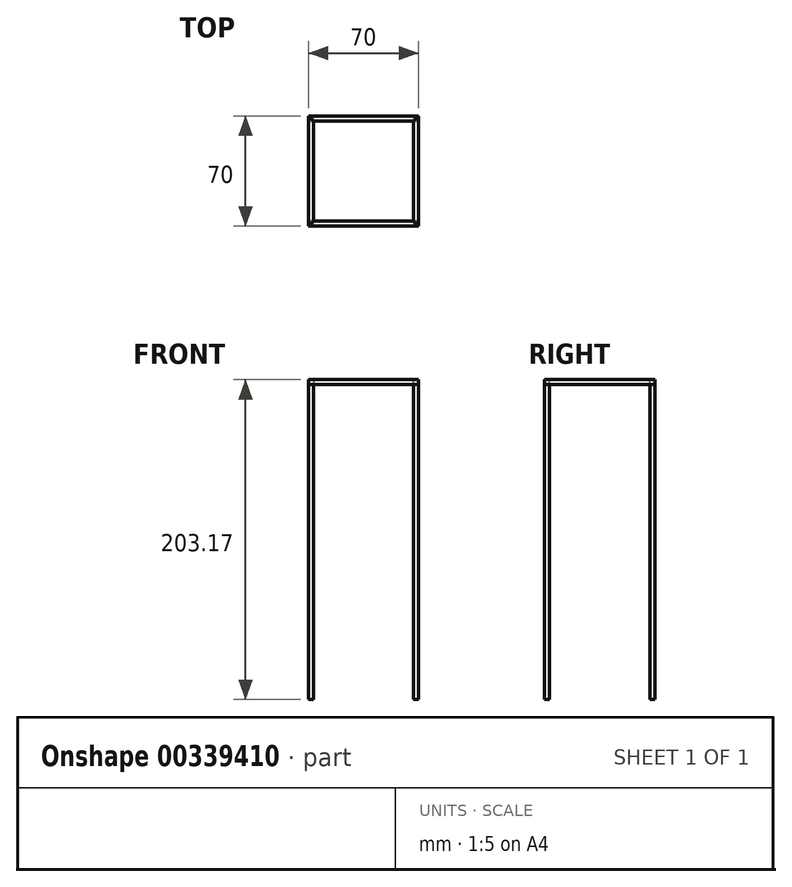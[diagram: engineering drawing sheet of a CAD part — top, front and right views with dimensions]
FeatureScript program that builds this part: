
annotation { "Feature Type Name" : "Feature", "Feature Type Description" : "" }
export const myFeature = defineFeature(function(context is Context, id is Id, definition is map)
    precondition{}
    {
        {
            var Q0;
            Q0=qCreatedBy(makeId("Front.planeOp"),FACE);
            var sketch = newSketch(context, id + "F0", { "sketchPlane" : qUnion([Q0])});
            skLineSegment(sketch, "E0.bottom", {"start": v(0, 200) * mm, "end": v(3.17, 200) * mm});
            skLineSegment(sketch, "E0.top", {"start": v(0, 0) * mm, "end": v(3.18, 0) * mm});
            skLineSegment(sketch, "E0.left", {"start": v(0, 200) * mm, "end": v(0, 0) * mm});
            skLineSegment(sketch, "E0.right", {"start": v(3.18, 200) * mm, "end": v(3.18, 0) * mm});
            skLineSegment(sketch, "E1.bottom", {"start": v(0, 203.18) * mm, "end": v(70, 203.18) * mm});
            skLineSegment(sketch, "E1.top", {"start": v(0, 200) * mm, "end": v(70, 200) * mm});
            skLineSegment(sketch, "E1.left", {"start": v(0, 203.18) * mm, "end": v(0, 200) * mm});
            skLineSegment(sketch, "E1.right", {"start": v(70, 203.18) * mm, "end": v(70, 200) * mm});
            skLineSegment(sketch, "E2", {"start": v(66.83, 200) * mm, "end": v(66.83, 0) * mm});
            skLineSegment(sketch, "E3", {"start": v(3.17, 196.8) * mm, "end": v(66.83, 190.43) * mm});
            skLineSegment(sketch, "E4", {"start": v(3.18, 200) * mm, "end": v(66.82, 193.62) * mm});
            skLineSegment(sketch, "E5", {"start": v(66.82, 193.62) * mm, "end": v(66.82, 190.43) * mm});
            skLineSegment(sketch, "E6", {"start": v(3.18, 196.8) * mm, "end": v(3.18, 200) * mm});
            skLineSegment(sketch, "E7", {"start": v(3.18, 100) * mm, "end": v(66.83, 100) * mm});
            skLineSegment(sketch, "E8", {"start": v(66.83, 103.17) * mm, "end": v(66.83, 100) * mm});
            skLineSegment(sketch, "E9", {"start": v(3.18, 100) * mm, "end": v(3.18, 103.17) * mm});
            skLineSegment(sketch, "E10", {"start": v(3.18, 183.7) * mm, "end": v(66.82, 151.36) * mm});
            skLineSegment(sketch, "E11", {"start": v(3.17, 187.25) * mm, "end": v(66.83, 154.92) * mm});
            skLineSegment(sketch, "E12", {"start": v(66.83, 154.92) * mm, "end": v(66.83, 151.36) * mm});
            skLineSegment(sketch, "E13", {"start": v(3.18, 183.7) * mm, "end": v(3.18, 187.25) * mm});
            skLineSegment(sketch, "E14.bottom", {"start": v(3.17, 190.43) * mm, "end": v(66.82, 190.43) * mm});
            skLineSegment(sketch, "E14.top", {"start": v(3.17, 187.25) * mm, "end": v(66.83, 187.25) * mm});
            skLineSegment(sketch, "E14.left", {"start": v(66.83, 190.43) * mm, "end": v(66.83, 187.25) * mm});
            skLineSegment(sketch, "E14.right", {"start": v(3.18, 190.43) * mm, "end": v(3.18, 187.25) * mm});
            skLineSegment(sketch, "E15.bottom", {"start": v(3.18, 144.4) * mm, "end": v(66.83, 103.18) * mm});
            skLineSegment(sketch, "E15.top", {"start": v(3.18, 148.18) * mm, "end": v(66.83, 106.96) * mm});
            skLineSegment(sketch, "E15.left", {"start": v(66.83, 106.96) * mm, "end": v(66.83, 103.17) * mm});
            skLineSegment(sketch, "E15.right", {"start": v(3.18, 148.18) * mm, "end": v(3.18, 144.4) * mm});
            skLineSegment(sketch, "E16.bottom", {"start": v(3.18, 148.18) * mm, "end": v(66.83, 148.18) * mm});
            skLineSegment(sketch, "E16.top", {"start": v(3.18, 151.36) * mm, "end": v(66.83, 151.36) * mm});
            skLineSegment(sketch, "E16.left", {"start": v(3.18, 151.36) * mm, "end": v(3.18, 148.18) * mm});
            skLineSegment(sketch, "E16.right", {"start": v(66.83, 151.36) * mm, "end": v(66.83, 148.18) * mm});
            skLineSegment(sketch, "E17", {"start": v(3.18, 103.17) * mm, "end": v(66.83, 103.17) * mm});
            skLineSegment(sketch, "E18", {"start": v(3.18, 100) * mm, "end": v(66.83, 8.34) * mm});
            skLineSegment(sketch, "E19", {"start": v(3.18, 100) * mm, "end": v(3.18, 91.66) * mm});
            skLineSegment(sketch, "E20", {"start": v(3.18, 91.66) * mm, "end": v(66.83, 0) * mm});
            skLineSegment(sketch, "E21", {"start": v(66.82, 0) * mm, "end": v(66.82, 8.34) * mm});
            skSolve(sketch);
        }
        {
            var Q0;
            Q0=makeQuery(id+"F0.imprint","IMPRINT",FACE,{"disambiguationData":[TD([[makeQuery(id+"F0.imprint","IMPRINT",EDGE,{"derivedFrom":sQuery(id+"F0.wireOp",EDGE,"E0.top")}),1.0]])]});
            extrude(context, id + "F1", {"entities" : qUnion([Q0]), "depth" : 3.17 * mm});
        }
        {
            var Q0;
            Q0=makeQuery(id+"F0.imprint","IMPRINT",FACE,{"disambiguationData":[TD([[makeQuery(id+"F0.imprint","IMPRINT",EDGE,{"derivedFrom":sQuery(id+"F0.wireOp",EDGE,"E1.bottom")}),-1.0]])]});
            extrude(context, id + "F2", {"entities" : qUnion([Q0]), "depth" : 3.17 * mm});
        }
        {
            var Q0;
            Q0=qCreatedBy(makeId("Front.planeOp"),FACE);
            cPlane(context, id + "F3", {"entities" : qUnion([Q0]), "cplaneType" : CPlaneType.OFFSET, "offset" : 35 * mm, "width" : 150 * mm, "height" : 150 * mm});
        }
        {
            var Q0;
            Q0=qCreatedBy(id+"F3.planeOp",FACE);
            var sketch = newSketch(context, id + "F4", { "sketchPlane" : qUnion([Q0])});
            skLineSegment(sketch, "E22", {"start": v(35, 200) * mm, "end": v(35, 0) * mm});
            skSolve(sketch);
        }
        {
            var Q0;
            Q0=makeQuery(id+"F2.opExtrude","CAP_EDGE",EDGE,{"disambiguationData":[OSD([sQuery(id+"F0.wireOp",EDGE,"E1.left")])],"isStart":false});
            var Q1;
            Q1=makeQuery(id+"F2.opExtrude","CAP_EDGE",EDGE,{"disambiguationData":[OSD([sQuery(id+"F0.wireOp",EDGE,"E1.right")])],"isStart":false});
            chamfer(context, id + "F5", {"entities" : qUnion([Q0, Q1]), "width" : 3.17 * mm, "tangentPropagation" : true});
        }
        {
            var Q0;
            Q0=makeQuery(id+"F1.opExtrude","SWEPT_BODY",BODY,{"disambiguationData":[OSD([sQuery(id+"F0.wireOp",EDGE,"E0.top"),sQuery(id+"F0.wireOp",EDGE,"E0.left"),sQuery(id+"F0.wireOp",EDGE,"E0.right"),sQuery(id+"F0.wireOp",EDGE,"E1.top")])]});
            var Q1;
            Q1=makeQuery(id+"F2.opExtrude","SWEPT_BODY",BODY,{"disambiguationData":[OSD([sQuery(id+"F0.wireOp",EDGE,"E1.bottom"),sQuery(id+"F0.wireOp",EDGE,"E1.top"),sQuery(id+"F0.wireOp",EDGE,"E1.left"),sQuery(id+"F0.wireOp",EDGE,"E1.right")])]});
            var Q2;
            Q2=sQuery(id+"F4.wireOp",EDGE,"E22");
            transform(context, id + "F6", {"entities" : qUnion([Q0, Q1]), "transformType" : TransformType.ROTATION, "transformAxis" : qUnion([Q2]), "angle" : 90 * degree, "makeCopy" : true});
        }
        {
            var Q0;
            Q0=makeQuery(id+"F1.opExtrude","SWEPT_BODY",BODY,{"disambiguationData":[OSD([sQuery(id+"F0.wireOp",EDGE,"E0.top"),sQuery(id+"F0.wireOp",EDGE,"E0.left"),sQuery(id+"F0.wireOp",EDGE,"E0.right"),sQuery(id+"F0.wireOp",EDGE,"E1.top")])]});
            var Q1;
            Q1=makeQuery(id+"F2.opExtrude","SWEPT_BODY",BODY,{"disambiguationData":[OSD([sQuery(id+"F0.wireOp",EDGE,"E1.bottom"),sQuery(id+"F0.wireOp",EDGE,"E1.top"),sQuery(id+"F0.wireOp",EDGE,"E1.left"),sQuery(id+"F0.wireOp",EDGE,"E1.right")])]});
            var Q2;
            Q2=makeQuery(id+"F6.opPattern","COPY",BODY,{"derivedFrom":makeQuery(id+"F1.opExtrude","SWEPT_BODY",BODY,{"disambiguationData":[OSD([sQuery(id+"F0.wireOp",EDGE,"E0.top"),sQuery(id+"F0.wireOp",EDGE,"E0.left"),sQuery(id+"F0.wireOp",EDGE,"E0.right"),sQuery(id+"F0.wireOp",EDGE,"E1.top")])]}),"instanceName":"1"});
            var Q3;
            Q3=makeQuery(id+"F6.opPattern","COPY",BODY,{"derivedFrom":makeQuery(id+"F2.opExtrude","SWEPT_BODY",BODY,{"disambiguationData":[OSD([sQuery(id+"F0.wireOp",EDGE,"E1.bottom"),sQuery(id+"F0.wireOp",EDGE,"E1.top"),sQuery(id+"F0.wireOp",EDGE,"E1.left"),sQuery(id+"F0.wireOp",EDGE,"E1.right")])]}),"instanceName":"1"});
            var Q4;
            Q4=sQuery(id+"F4.wireOp",EDGE,"E22");
            transform(context, id + "F7", {"entities" : qUnion([Q0, Q1, Q2, Q3]), "transformType" : TransformType.ROTATION, "transformAxis" : qUnion([Q4]), "angle" : 180 * degree, "makeCopy" : true});
        }
    });
